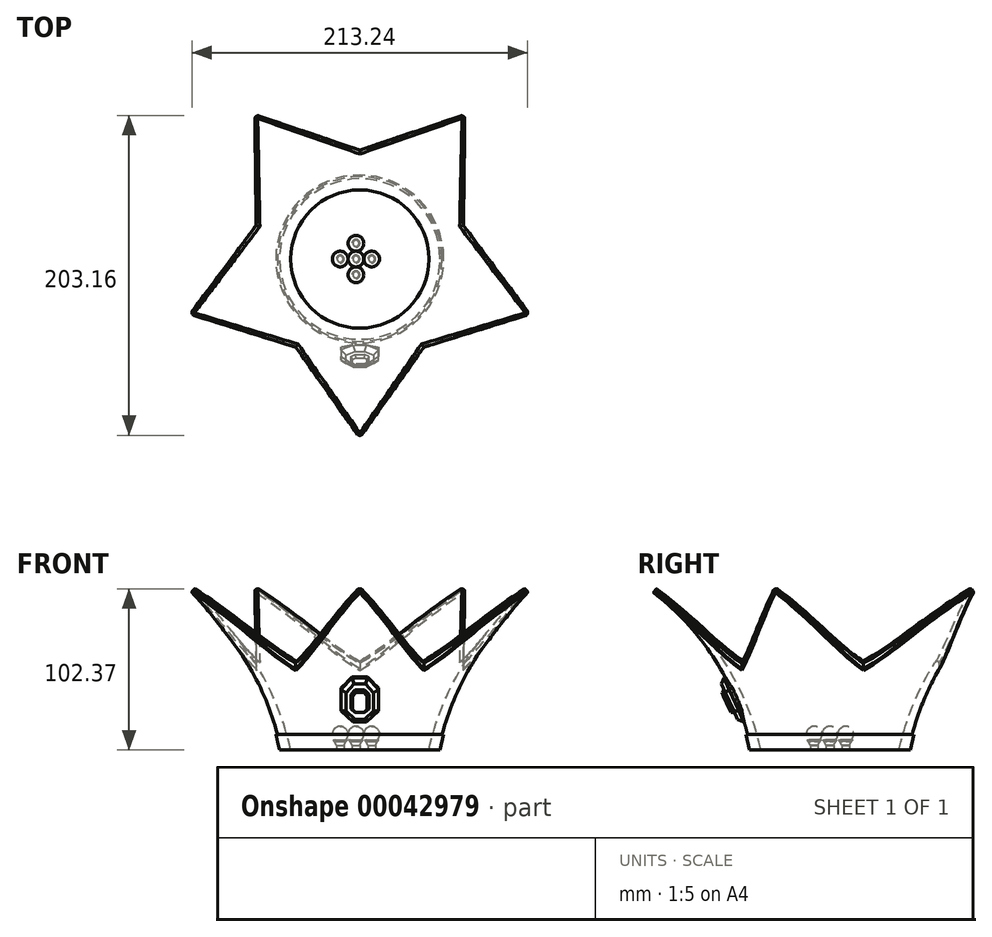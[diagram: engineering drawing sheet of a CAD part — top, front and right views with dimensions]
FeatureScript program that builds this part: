
annotation { "Feature Type Name" : "Feature", "Feature Type Description" : "" }
export const myFeature = defineFeature(function(context is Context, id is Id, definition is map)
    precondition{}
    {
        {
            var Q0;
            Q0=qCreatedBy(makeId("Front.planeOp"),FACE);
            var sketch = newSketch(context, id + "F0", { "sketchPlane" : qUnion([Q0])});
            skLineSegment(sketch, "E0", {"start": v(0, 0) * mm, "end": v(0, 100) * mm, "construction": true});
            skLineSegment(sketch, "E1", {"start": v(0, 0) * mm, "end": v(-50, 0) * mm, "construction": true});
            skArc(sketch, "E2", {"start": v(-50, 0) * mm, "mid": v(-71.94, 55.6) * mm, "end": v(-111.98, 100) * mm});
            skLineSegment(sketch, "E3", {"start": v(-111.98, 100) * mm, "end": v(-214.57, -32.8) * mm, "construction": true});
            skLineSegment(sketch, "E4", {"start": v(-111.98, 100) * mm, "end": v(-110.15, 102.37) * mm});
            skArc(sketch, "E5", {"start": v(-43.88, 0) * mm, "mid": v(-67.74, 57.2) * mm, "end": v(-110.15, 102.37) * mm});
            skLineSegment(sketch, "E6", {"start": v(-50, 0) * mm, "end": v(-43.88, 0) * mm});
            skLineSegment(sketch, "E7", {"start": v(-50, 0) * mm, "end": v(-51, 0) * mm});
            skLineSegment(sketch, "E8", {"start": v(-52.31, 10) * mm, "end": v(-53.31, 10) * mm});
            skLineSegment(sketch, "E9", {"start": v(-53.31, 10) * mm, "end": v(-51, 0) * mm});
            skLineSegment(sketch, "E10", {"start": v(-53.31, 10) * mm, "end": v(-53.31, 0) * mm, "construction": true});
            skSolve(sketch);
        }
        {
            var Q0;
            Q0=qSketchRegion(id+"F0",true);
            var Q1;
            Q1=sQuery(id+"F0.wireOp",EDGE,"E0");
            revolve(context, id + "F1", {"entities" : qUnion([Q0]), "axis" : qUnion([Q1]), "revolveType" : RevolveType.FULL});
        }
        {
            var Q0;
            Q0=qCreatedBy(makeId("Top.planeOp"),FACE);
            var sketch = newSketch(context, id + "F2", { "sketchPlane" : qUnion([Q0])});
            skLineSegment(sketch, "E11", {"start": v(0, 0) * mm, "end": v(0, -111.98) * mm, "construction": true});
            skCircle(sketch, "E12.0", {"center": v(0, 0) * mm, "radius": 111.98 * mm, "construction": true});
            skLineSegment(sketch, "E13", {"start": v(-1, -111.98) * mm, "end": v(1, -111.98) * mm});
            skLineSegment(sketch, "E14", {"start": v(-1, -111.98) * mm, "end": v(-40.68, -56) * mm});
            skPoint(sketch, "E15", {"position": v(0, -56) * mm});
            skLineSegment(sketch, "E16.MirrorCS", {"start": v(1, -111.98) * mm, "end": v(40.68, -56) * mm});
            skLineSegment(sketch, "E17.1.0", {"start": v(106.2, -35.56) * mm, "end": v(106.8, -33.65) * mm});
            skLineSegment(sketch, "E17.1.1", {"start": v(106.2, -35.56) * mm, "end": v(40.68, -56) * mm});
            skLineSegment(sketch, "E17.1.2", {"start": v(106.8, -33.65) * mm, "end": v(65.82, 21.39) * mm});
            skLineSegment(sketch, "E17.2.0", {"start": v(66.63, 90) * mm, "end": v(65.01, 91.18) * mm});
            skLineSegment(sketch, "E17.2.1", {"start": v(66.63, 90) * mm, "end": v(65.82, 21.39) * mm});
            skLineSegment(sketch, "E17.2.2", {"start": v(65.01, 91.18) * mm, "end": v(0, 69.2) * mm});
            skLineSegment(sketch, "E17.3.0", {"start": v(-65.01, 91.18) * mm, "end": v(-66.63, 90) * mm});
            skLineSegment(sketch, "E17.3.1", {"start": v(-65.01, 91.18) * mm, "end": v(0, 69.2) * mm});
            skLineSegment(sketch, "E17.3.2", {"start": v(-66.63, 90) * mm, "end": v(-65.82, 21.39) * mm});
            skLineSegment(sketch, "E17.4.0", {"start": v(-106.8, -33.65) * mm, "end": v(-106.2, -35.56) * mm});
            skLineSegment(sketch, "E17.4.1", {"start": v(-106.8, -33.65) * mm, "end": v(-65.82, 21.39) * mm});
            skLineSegment(sketch, "E17.4.2", {"start": v(-106.2, -35.56) * mm, "end": v(-40.68, -56) * mm});
            skCircle(sketch, "E18", {"center": v(0, 0) * mm, "radius": 111.99 * mm});
            skCircle(sketch, "E19.0", {"center": v(0, 0) * mm, "radius": 51 * mm, "construction": true});
            skPoint(sketch, "E20", {"position": v(0, -51) * mm});
            skLineSegment(sketch, "E21", {"start": v(0, -56) * mm, "end": v(0, -67) * mm, "construction": true});
            skSolve(sketch);
        }
        {
            var Q0;
            {var subQ2=sQuery(id+"F2.wireOp",EDGE,"E14");Q0=makeQuery(id+"F2.imprint","IMPRINT",FACE,{"disambiguationData":[TD([[makeQuery(id+"F2.imprint","IMPRINT",EDGE,{"derivedFrom":subQ2}),1.0]])]});}
            var Q1;
            {var subQ2=sQuery(id+"F2.wireOp",EDGE,"E16.MirrorCS");Q1=makeQuery(id+"F2.imprint","IMPRINT",FACE,{"disambiguationData":[TD([[makeQuery(id+"F2.imprint","IMPRINT",EDGE,{"derivedFrom":subQ2}),-1.0]])]});}
            var Q2;
            {var subQ2=sQuery(id+"F2.wireOp",EDGE,"E17.1.2");Q2=makeQuery(id+"F2.imprint","IMPRINT",FACE,{"disambiguationData":[TD([[makeQuery(id+"F2.imprint","IMPRINT",EDGE,{"derivedFrom":subQ2}),-1.0]])]});}
            var Q3;
            {var subQ2=sQuery(id+"F2.wireOp",EDGE,"E17.3.2");Q3=makeQuery(id+"F2.imprint","IMPRINT",FACE,{"disambiguationData":[TD([[makeQuery(id+"F2.imprint","IMPRINT",EDGE,{"derivedFrom":subQ2}),-1.0]])]});}
            var Q4;
            {var subQ2=sQuery(id+"F2.wireOp",EDGE,"E17.2.2");Q4=makeQuery(id+"F2.imprint","IMPRINT",FACE,{"disambiguationData":[TD([[makeQuery(id+"F2.imprint","IMPRINT",EDGE,{"derivedFrom":subQ2}),-1.0]])]});}
            extrude(context, id + "F3", {"entities" : qUnion([Q0, Q1, Q2, Q3, Q4]), "operationType" : NewBodyOperationType.REMOVE, "endBound" : BoundingType.THROUGH_ALL, "depth" : 25 * mm});
        }
        {
            var Q0;
            Q0=makeQuery(id+"F3.boolean.opBoolean","INTERSECT",VERTEX,{"derivedFrom":[makeQuery(id+"F1.opRevolve","SWEPT_FACE",FACE,{"disambiguationData":[OSD([sQuery(id+"F0.wireOp",EDGE,"E2")])]}),makeQuery(id+"F1.opRevolve","SWEPT_FACE",FACE,{"disambiguationData":[OSD([sQuery(id+"F0.wireOp",EDGE,"E4")])]}),makeQuery(id+"F3.opExtrude","SWEPT_FACE",FACE,{"disambiguationData":[OSD([sQuery(id+"F2.wireOp",EDGE,"E14")])]})]});
            var Q1;
            Q1=makeQuery(id+"F3.boolean.opBoolean","INTERSECT",VERTEX,{"derivedFrom":[makeQuery(id+"F1.opRevolve","SWEPT_FACE",FACE,{"disambiguationData":[OSD([sQuery(id+"F0.wireOp",EDGE,"E2")])]}),makeQuery(id+"F1.opRevolve","SWEPT_FACE",FACE,{"disambiguationData":[OSD([sQuery(id+"F0.wireOp",EDGE,"E4")])]}),makeQuery(id+"F3.opExtrude","SWEPT_FACE",FACE,{"disambiguationData":[OSD([sQuery(id+"F2.wireOp",EDGE,"E16.MirrorCS")])]})]});
            var Q2;
            Q2=sQuery(id+"F2.wireOp",VERTEX,"E21.end");
            cPlane(context, id + "F4", {"entities" : qUnion([Q0, Q1, Q2]), "cplaneType" : CPlaneType.THREE_POINT, "offset" : 150 * mm, "width" : 150 * mm, "height" : 150 * mm});
        }
        {
            var Q0;
            Q0=qCreatedBy(id+"F4.planeOp",FACE);
            cPlane(context, id + "F5", {"entities" : qUnion([Q0]), "cplaneType" : CPlaneType.OFFSET, "offset" : 20 * mm, "oppositeDirection" : true, "width" : 150 * mm, "height" : 150 * mm});
        }
        {
            var Q0;
            Q0=qCreatedBy(id+"F5.planeOp",FACE);
            var sketch = newSketch(context, id + "F6", { "sketchPlane" : qUnion([Q0])});
            skLineSegment(sketch, "E22.0", {"start": v(0, 0) * mm, "end": v(0, 91.2) * mm, "construction": true});
            skLineSegment(sketch, "E23.0", {"start": v(-1, 45.94) * mm, "end": v(1, 45.94) * mm, "construction": true});
            skPoint(sketch, "E24.0", {"position": v(-40.68, 69.52) * mm});
            skPoint(sketch, "E25.0", {"position": v(40.68, 69.52) * mm});
            skLineSegment(sketch, "E26", {"start": v(-40.68, 69.52) * mm, "end": v(40.68, 69.52) * mm, "construction": true});
            skLineSegment(sketch, "E27", {"start": v(-5, 69.52) * mm, "end": v(5, 69.52) * mm});
            skPoint(sketch, "E28", {"position": v(0, 69.52) * mm});
            skLineSegment(sketch, "E29", {"start": v(-5, 69.52) * mm, "end": v(-11.83, 61.33) * mm});
            skLineSegment(sketch, "E30", {"start": v(-11.83, 61.33) * mm, "end": v(-11.83, 46.33) * mm});
            skLineSegment(sketch, "E31", {"start": v(-11.83, 46.33) * mm, "end": v(-4.17, 38.9) * mm});
            skLineSegment(sketch, "E32", {"start": v(-4.17, 38.9) * mm, "end": v(0, 38.9) * mm});
            skLineSegment(sketch, "E33.MirrorCS", {"start": v(5, 69.52) * mm, "end": v(11.83, 61.33) * mm});
            skLineSegment(sketch, "E34.MirrorCS", {"start": v(11.83, 61.33) * mm, "end": v(11.83, 46.33) * mm});
            skLineSegment(sketch, "E35.MirrorCS", {"start": v(11.83, 46.33) * mm, "end": v(4.17, 38.9) * mm});
            skLineSegment(sketch, "E36.MirrorCS", {"start": v(4.17, 38.9) * mm, "end": v(0, 38.9) * mm});
            skSolve(sketch);
        }
        {
            var Q0;
            Q0=qSketchRegion(id+"F6",true);
            extrude(context, id + "F7", {"entities" : qUnion([Q0]), "operationType" : NewBodyOperationType.ADD, "depth" : 4.5 * mm, "hasSecondDirection" : true, "secondDirectionOppositeDirection" : true, "secondDirectionDepth" : 1 * mm});
        }
        {
            var Q0;
            Q0=makeQuery(id+"F7.opExtrude","CAP_EDGE",EDGE,{"disambiguationData":[OSD([sQuery(id+"F6.wireOp",EDGE,"E27")])],"isStart":false});
            var Q1;
            Q1=makeQuery(id+"F7.opExtrude","CAP_EDGE",EDGE,{"disambiguationData":[OSD([sQuery(id+"F6.wireOp",EDGE,"E29")])],"isStart":false});
            var Q2;
            Q2=makeQuery(id+"F7.opExtrude","CAP_EDGE",EDGE,{"disambiguationData":[OSD([sQuery(id+"F6.wireOp",EDGE,"E33.MirrorCS")])],"isStart":false});
            var Q3;
            Q3=makeQuery(id+"F7.opExtrude","CAP_EDGE",EDGE,{"disambiguationData":[OSD([sQuery(id+"F6.wireOp",EDGE,"E34.MirrorCS")])],"isStart":false});
            var Q4;
            Q4=makeQuery(id+"F7.opExtrude","CAP_EDGE",EDGE,{"disambiguationData":[OSD([sQuery(id+"F6.wireOp",EDGE,"E35.MirrorCS")])],"isStart":false});
            var Q5;
            Q5=makeQuery(id+"F7.opExtrude","CAP_EDGE",EDGE,{"disambiguationData":[OSD([sQuery(id+"F6.wireOp",EDGE,"E31")])],"isStart":false});
            var Q6;
            Q6=makeQuery(id+"F7.opExtrude","CAP_EDGE",EDGE,{"disambiguationData":[OSD([sQuery(id+"F6.wireOp",EDGE,"E32"),sQuery(id+"F6.wireOp",EDGE,"E36.MirrorCS")])],"isStart":false});
            var Q7;
            Q7=makeQuery(id+"F7.opExtrude","CAP_EDGE",EDGE,{"disambiguationData":[OSD([sQuery(id+"F6.wireOp",EDGE,"E30")])],"isStart":false});
            chamfer(context, id + "F8", {"entities" : qUnion([Q0, Q1, Q2, Q3, Q4, Q5, Q6, Q7]), "width" : 3 * mm, "tangentPropagation" : true});
        }
        {
            var Q0;
            Q0=makeQuery(id+"F7.opExtrude","CAP_FACE",FACE,{"disambiguationData":[OSD([sQuery(id+"F6.wireOp",EDGE,"E27"),sQuery(id+"F6.wireOp",EDGE,"E29"),sQuery(id+"F6.wireOp",EDGE,"E30"),sQuery(id+"F6.wireOp",EDGE,"E31"),sQuery(id+"F6.wireOp",EDGE,"E32"),sQuery(id+"F6.wireOp",EDGE,"E33.MirrorCS"),sQuery(id+"F6.wireOp",EDGE,"E34.MirrorCS"),sQuery(id+"F6.wireOp",EDGE,"E35.MirrorCS"),sQuery(id+"F6.wireOp",EDGE,"E36.MirrorCS")])],"isStart":false});
            var sketch = newSketch(context, id + "F9", { "sketchPlane" : qUnion([Q0])});
            skLineSegment(sketch, "E37", {"start": v(-3, 62.47) * mm, "end": v(0, 62.47) * mm});
            skLineSegment(sketch, "E38", {"start": v(-3, 62.47) * mm, "end": v(-5.72, 59.21) * mm});
            skLineSegment(sketch, "E39", {"start": v(-5.72, 49.21) * mm, "end": v(-3, 46.58) * mm});
            skLineSegment(sketch, "E40", {"start": v(-3, 46.58) * mm, "end": v(0, 46.58) * mm});
            skLineSegment(sketch, "E41", {"start": v(0, 66.52) * mm, "end": v(0, 41.9) * mm, "construction": true});
            skLineSegment(sketch, "E42", {"start": v(-5.72, 54.21) * mm, "end": v(0, 54.21) * mm, "construction": true});
            skLineSegment(sketch, "E43", {"start": v(-5.72, 59.21) * mm, "end": v(-5.72, 49.21) * mm});
            skLineSegment(sketch, "E44.MirrorCS", {"start": v(3, 62.47) * mm, "end": v(0, 62.47) * mm});
            skLineSegment(sketch, "E45.MirrorCS", {"start": v(3, 62.47) * mm, "end": v(5.72, 59.21) * mm});
            skLineSegment(sketch, "E46.MirrorCS", {"start": v(5.72, 59.21) * mm, "end": v(5.72, 49.21) * mm});
            skLineSegment(sketch, "E47.MirrorCS", {"start": v(5.72, 49.21) * mm, "end": v(3, 46.58) * mm});
            skLineSegment(sketch, "E48.MirrorCS", {"start": v(3, 46.58) * mm, "end": v(0, 46.58) * mm});
            skSolve(sketch);
        }
        {
            var Q0;
            Q0=makeQuery(id+"F9.imprint","IMPRINT",FACE,{"disambiguationData":[TD([[makeQuery(id+"F9.imprint","IMPRINT",EDGE,{"derivedFrom":sQuery(id+"F9.wireOp",EDGE,"E37")}),1.0]])]});
            cPlane(context, id + "F10", {"entities" : qUnion([Q0]), "cplaneType" : CPlaneType.OFFSET, "offset" : 2 * mm, "width" : 150 * mm, "height" : 150 * mm});
        }
        {
            var Q0;
            Q0=qCreatedBy(id+"F10.planeOp",FACE);
            var sketch = newSketch(context, id + "F11", { "sketchPlane" : qUnion([Q0])});
            skLineSegment(sketch, "E49.0", {"start": v(-3, 62.47) * mm, "end": v(-5.72, 59.21) * mm, "construction": true});
            skLineSegment(sketch, "E50.0", {"start": v(-3, 62.47) * mm, "end": v(0, 62.47) * mm, "construction": true});
            skLineSegment(sketch, "E51.0", {"start": v(3, 62.47) * mm, "end": v(0, 62.47) * mm, "construction": true});
            skLineSegment(sketch, "E52.0", {"start": v(3, 62.47) * mm, "end": v(5.72, 59.21) * mm, "construction": true});
            skLineSegment(sketch, "E53.0", {"start": v(5.72, 59.21) * mm, "end": v(5.72, 49.21) * mm, "construction": true});
            skLineSegment(sketch, "E54.0", {"start": v(5.72, 49.21) * mm, "end": v(3, 46.58) * mm, "construction": true});
            skLineSegment(sketch, "E55.0", {"start": v(3, 46.58) * mm, "end": v(0, 46.58) * mm, "construction": true});
            skLineSegment(sketch, "E56.0", {"start": v(-3, 46.58) * mm, "end": v(0, 46.58) * mm, "construction": true});
            skLineSegment(sketch, "E57.0", {"start": v(-5.72, 49.21) * mm, "end": v(-3, 46.58) * mm, "construction": true});
            skLineSegment(sketch, "E58.0", {"start": v(-5.72, 59.21) * mm, "end": v(-5.72, 49.21) * mm, "construction": true});
            skLineSegment(sketch, "E59.0", {"start": v(-2.53, 61.47) * mm, "end": v(0, 61.47) * mm});
            skLineSegment(sketch, "E59.1", {"start": v(2.53, 61.47) * mm, "end": v(0, 61.47) * mm});
            skLineSegment(sketch, "E59.2", {"start": v(-2.53, 61.47) * mm, "end": v(-4.72, 58.85) * mm});
            skLineSegment(sketch, "E59.3", {"start": v(2.53, 61.47) * mm, "end": v(4.72, 58.85) * mm});
            skLineSegment(sketch, "E59.4", {"start": v(4.72, 58.85) * mm, "end": v(4.72, 49.63) * mm});
            skLineSegment(sketch, "E59.5", {"start": v(4.72, 49.63) * mm, "end": v(2.6, 47.58) * mm});
            skLineSegment(sketch, "E59.6", {"start": v(-4.72, 58.85) * mm, "end": v(-4.72, 49.63) * mm});
            skLineSegment(sketch, "E59.7", {"start": v(-4.72, 49.63) * mm, "end": v(-2.6, 47.58) * mm});
            skLineSegment(sketch, "E59.8", {"start": v(-2.6, 47.58) * mm, "end": v(0, 47.58) * mm});
            skLineSegment(sketch, "E59.9", {"start": v(2.6, 47.58) * mm, "end": v(0, 47.58) * mm});
            skSolve(sketch);
        }
        {
            var Q1;
            Q1=makeQuery(id+"F9.imprint","IMPRINT",FACE,{"disambiguationData":[TD([[makeQuery(id+"F9.imprint","IMPRINT",EDGE,{"derivedFrom":sQuery(id+"F9.wireOp",EDGE,"E37")}),-1.0]])]});
            var Q2;
            Q2=makeQuery(id+"F11.imprint","IMPRINT",FACE,{"disambiguationData":[TD([[makeQuery(id+"F11.imprint","IMPRINT",EDGE,{"derivedFrom":sQuery(id+"F11.wireOp",EDGE,"E59.0")}),-1.0]])]});
            loft(context, id + "F12", {"operationType" : NewBodyOperationType.ADD, "sheetProfilesArray" : [{ "sheetProfileEntities" : qUnion([Q1]) }, { "sheetProfileEntities" : qUnion([Q2]) }]});
        }
        {
            var Q0;
            Q0=makeQuery(id+"F3.boolean.opBoolean","INTERSECT",EDGE,{"derivedFrom":[makeQuery(id+"F1.opRevolve","SWEPT_FACE",FACE,{"disambiguationData":[OSD([sQuery(id+"F0.wireOp",EDGE,"E2")])]}),makeQuery(id+"F3.opExtrude","SWEPT_FACE",FACE,{"disambiguationData":[OSD([sQuery(id+"F2.wireOp",EDGE,"E16.MirrorCS")])]})]});
            var Q1;
            Q1=makeQuery(id+"F3.boolean.opBoolean","INTERSECT",EDGE,{"derivedFrom":[makeQuery(id+"F1.opRevolve","SWEPT_FACE",FACE,{"disambiguationData":[OSD([sQuery(id+"F0.wireOp",EDGE,"E2")])]}),makeQuery(id+"F3.opExtrude","SWEPT_FACE",FACE,{"disambiguationData":[OSD([sQuery(id+"F2.wireOp",EDGE,"E14")])]})]});
            var Q2;
            Q2=makeQuery(id+"F3.boolean.opBoolean","INTERSECT",EDGE,{"derivedFrom":[makeQuery(id+"F1.opRevolve","SWEPT_FACE",FACE,{"disambiguationData":[OSD([sQuery(id+"F0.wireOp",EDGE,"E5")])]}),makeQuery(id+"F3.opExtrude","SWEPT_FACE",FACE,{"disambiguationData":[OSD([sQuery(id+"F2.wireOp",EDGE,"E14")])]})]});
            var Q3;
            Q3=makeQuery(id+"F3.boolean.opBoolean","INTERSECT",EDGE,{"derivedFrom":[makeQuery(id+"F1.opRevolve","SWEPT_FACE",FACE,{"disambiguationData":[OSD([sQuery(id+"F0.wireOp",EDGE,"E5")])]}),makeQuery(id+"F3.opExtrude","SWEPT_FACE",FACE,{"disambiguationData":[OSD([sQuery(id+"F2.wireOp",EDGE,"E16.MirrorCS")])]})]});
            var Q4;
            Q4=makeQuery(id+"F3.boolean.opBoolean","INTERSECT",EDGE,{"derivedFrom":[makeQuery(id+"F1.opRevolve","SWEPT_FACE",FACE,{"disambiguationData":[OSD([sQuery(id+"F0.wireOp",EDGE,"E2")])]}),makeQuery(id+"F3.opExtrude","SWEPT_FACE",FACE,{"disambiguationData":[OSD([sQuery(id+"F2.wireOp",EDGE,"E17.4.2")])]})]});
            var Q5;
            Q5=makeQuery(id+"F3.boolean.opBoolean","INTERSECT",EDGE,{"derivedFrom":[makeQuery(id+"F1.opRevolve","SWEPT_FACE",FACE,{"disambiguationData":[OSD([sQuery(id+"F0.wireOp",EDGE,"E5")])]}),makeQuery(id+"F3.opExtrude","SWEPT_FACE",FACE,{"disambiguationData":[OSD([sQuery(id+"F2.wireOp",EDGE,"E17.4.2")])]})]});
            var Q6;
            Q6=makeQuery(id+"F3.boolean.opBoolean","INTERSECT",EDGE,{"derivedFrom":[makeQuery(id+"F1.opRevolve","SWEPT_FACE",FACE,{"disambiguationData":[OSD([sQuery(id+"F0.wireOp",EDGE,"E2")])]}),makeQuery(id+"F3.opExtrude","SWEPT_FACE",FACE,{"disambiguationData":[OSD([sQuery(id+"F2.wireOp",EDGE,"E17.4.1")])]})]});
            var Q7;
            Q7=makeQuery(id+"F3.boolean.opBoolean","INTERSECT",EDGE,{"derivedFrom":[makeQuery(id+"F1.opRevolve","SWEPT_FACE",FACE,{"disambiguationData":[OSD([sQuery(id+"F0.wireOp",EDGE,"E5")])]}),makeQuery(id+"F3.opExtrude","SWEPT_FACE",FACE,{"disambiguationData":[OSD([sQuery(id+"F2.wireOp",EDGE,"E17.4.1")])]})]});
            var Q8;
            Q8=makeQuery(id+"F3.boolean.opBoolean","INTERSECT",EDGE,{"derivedFrom":[makeQuery(id+"F1.opRevolve","SWEPT_FACE",FACE,{"disambiguationData":[OSD([sQuery(id+"F0.wireOp",EDGE,"E2")])]}),makeQuery(id+"F3.opExtrude","SWEPT_FACE",FACE,{"disambiguationData":[OSD([sQuery(id+"F2.wireOp",EDGE,"E17.3.2")])]})]});
            var Q9;
            Q9=makeQuery(id+"F3.boolean.opBoolean","INTERSECT",EDGE,{"derivedFrom":[makeQuery(id+"F1.opRevolve","SWEPT_FACE",FACE,{"disambiguationData":[OSD([sQuery(id+"F0.wireOp",EDGE,"E5")])]}),makeQuery(id+"F3.opExtrude","SWEPT_FACE",FACE,{"disambiguationData":[OSD([sQuery(id+"F2.wireOp",EDGE,"E17.3.2")])]})]});
            var Q10;
            Q10=makeQuery(id+"F3.boolean.opBoolean","INTERSECT",EDGE,{"derivedFrom":[makeQuery(id+"F1.opRevolve","SWEPT_FACE",FACE,{"disambiguationData":[OSD([sQuery(id+"F0.wireOp",EDGE,"E5")])]}),makeQuery(id+"F3.opExtrude","SWEPT_FACE",FACE,{"disambiguationData":[OSD([sQuery(id+"F2.wireOp",EDGE,"E17.1.1")])]})]});
            var Q11;
            Q11=makeQuery(id+"F3.boolean.opBoolean","INTERSECT",EDGE,{"derivedFrom":[makeQuery(id+"F1.opRevolve","SWEPT_FACE",FACE,{"disambiguationData":[OSD([sQuery(id+"F0.wireOp",EDGE,"E2")])]}),makeQuery(id+"F3.opExtrude","SWEPT_FACE",FACE,{"disambiguationData":[OSD([sQuery(id+"F2.wireOp",EDGE,"E17.1.1")])]})]});
            var Q12;
            Q12=makeQuery(id+"F3.boolean.opBoolean","INTERSECT",EDGE,{"derivedFrom":[makeQuery(id+"F1.opRevolve","SWEPT_FACE",FACE,{"disambiguationData":[OSD([sQuery(id+"F0.wireOp",EDGE,"E5")])]}),makeQuery(id+"F3.opExtrude","SWEPT_FACE",FACE,{"disambiguationData":[OSD([sQuery(id+"F2.wireOp",EDGE,"E17.1.2")])]})]});
            var Q13;
            Q13=makeQuery(id+"F3.boolean.opBoolean","INTERSECT",EDGE,{"derivedFrom":[makeQuery(id+"F1.opRevolve","SWEPT_FACE",FACE,{"disambiguationData":[OSD([sQuery(id+"F0.wireOp",EDGE,"E2")])]}),makeQuery(id+"F3.opExtrude","SWEPT_FACE",FACE,{"disambiguationData":[OSD([sQuery(id+"F2.wireOp",EDGE,"E17.1.2")])]})]});
            var Q14;
            Q14=makeQuery(id+"F3.boolean.opBoolean","INTERSECT",EDGE,{"derivedFrom":[makeQuery(id+"F1.opRevolve","SWEPT_FACE",FACE,{"disambiguationData":[OSD([sQuery(id+"F0.wireOp",EDGE,"E2")])]}),makeQuery(id+"F3.opExtrude","SWEPT_FACE",FACE,{"disambiguationData":[OSD([sQuery(id+"F2.wireOp",EDGE,"E17.2.1")])]})]});
            var Q15;
            Q15=makeQuery(id+"F3.boolean.opBoolean","INTERSECT",EDGE,{"derivedFrom":[makeQuery(id+"F1.opRevolve","SWEPT_FACE",FACE,{"disambiguationData":[OSD([sQuery(id+"F0.wireOp",EDGE,"E5")])]}),makeQuery(id+"F3.opExtrude","SWEPT_FACE",FACE,{"disambiguationData":[OSD([sQuery(id+"F2.wireOp",EDGE,"E17.2.1")])]})]});
            var Q16;
            Q16=makeQuery(id+"F3.boolean.opBoolean","INTERSECT",EDGE,{"derivedFrom":[makeQuery(id+"F1.opRevolve","SWEPT_FACE",FACE,{"disambiguationData":[OSD([sQuery(id+"F0.wireOp",EDGE,"E2")])]}),makeQuery(id+"F3.opExtrude","SWEPT_FACE",FACE,{"disambiguationData":[OSD([sQuery(id+"F2.wireOp",EDGE,"E17.2.2")])]})]});
            var Q17;
            Q17=makeQuery(id+"F3.boolean.opBoolean","INTERSECT",EDGE,{"derivedFrom":[makeQuery(id+"F1.opRevolve","SWEPT_FACE",FACE,{"disambiguationData":[OSD([sQuery(id+"F0.wireOp",EDGE,"E5")])]}),makeQuery(id+"F3.opExtrude","SWEPT_FACE",FACE,{"disambiguationData":[OSD([sQuery(id+"F2.wireOp",EDGE,"E17.2.2")])]})]});
            var Q18;
            Q18=makeQuery(id+"F3.boolean.opBoolean","INTERSECT",EDGE,{"derivedFrom":[makeQuery(id+"F1.opRevolve","SWEPT_FACE",FACE,{"disambiguationData":[OSD([sQuery(id+"F0.wireOp",EDGE,"E2")])]}),makeQuery(id+"F3.opExtrude","SWEPT_FACE",FACE,{"disambiguationData":[OSD([sQuery(id+"F2.wireOp",EDGE,"E17.3.1")])]})]});
            var Q19;
            Q19=makeQuery(id+"F3.boolean.opBoolean","INTERSECT",EDGE,{"derivedFrom":[makeQuery(id+"F1.opRevolve","SWEPT_FACE",FACE,{"disambiguationData":[OSD([sQuery(id+"F0.wireOp",EDGE,"E5")])]}),makeQuery(id+"F3.opExtrude","SWEPT_FACE",FACE,{"disambiguationData":[OSD([sQuery(id+"F2.wireOp",EDGE,"E17.3.1")])]})]});
            fillet(context, id + "F13", {"entities" : qUnion([Q0, Q1, Q2, Q3, Q4, Q5, Q6, Q7, Q8, Q9, Q10, Q11, Q12, Q13, Q14, Q15, Q16, Q17, Q18, Q19]), "radius" : 1.3 * mm, "tangentPropagation" : true, "allowEdgeOverflow" : false});
        }
        {
            var Q0;
            Q0=qCreatedBy(makeId("Front.planeOp"),FACE);
            var sketch = newSketch(context, id + "F14", { "sketchPlane" : qUnion([Q0])});
            skPoint(sketch, "E60.0", {"position": v(0, 0) * mm});
            skPoint(sketch, "E61.0", {"position": v(-4.9, 0) * mm});
            skLineSegment(sketch, "E62", {"start": v(0, 0) * mm, "end": v(-4.9, 0) * mm, "construction": true});
            skLineSegment(sketch, "E63", {"start": v(-2.45, 0) * mm, "end": v(-2.45, 15) * mm});
            skLineSegment(sketch, "E64", {"start": v(-2.45, 0) * mm, "end": v(0, 0) * mm});
            skLineSegment(sketch, "E65", {"start": v(0, 0) * mm, "end": v(0, 3) * mm});
            skArc(sketch, "E66", {"start": v(2.13, 6.53) * mm, "mid": v(0.94, 4.84) * mm, "end": v(0, 3) * mm});
            skArc(sketch, "E67", {"start": v(-0.49, 5.4) * mm, "mid": v(0.88, 5.83) * mm, "end": v(2.13, 6.53) * mm});
            skArc(sketch, "E68", {"start": v(-0.49, 5.4) * mm, "mid": v(2.45, 11) * mm, "end": v(-2.45, 15) * mm});
            skLineSegment(sketch, "E69", {"start": v(-0.49, 5.4) * mm, "end": v(-2.45, 5) * mm, "construction": true});
            skLineSegment(sketch, "E70", {"start": v(0, 3) * mm, "end": v(-0.49, 5.4) * mm, "construction": true});
            skSolve(sketch);
        }
        {
            var Q0;
            Q0=makeQuery(id+"F14.imprint","IMPRINT",FACE,{"disambiguationData":[TD([[makeQuery(id+"F14.imprint","IMPRINT",EDGE,{"derivedFrom":sQuery(id+"F14.wireOp",EDGE,"E63")}),-1.0]])]});
            var Q1;
            Q1=sQuery(id+"F14.wireOp",EDGE,"E63");
            revolve(context, id + "F15", {"entities" : qUnion([Q0]), "axis" : qUnion([Q1]), "revolveType" : RevolveType.FULL});
        }
        {
            var Q0;
            Q0=makeQuery(id+"F15.opRevolve","SWEPT_BODY",BODY,{"disambiguationData":[OSD([sQuery(id+"F14.wireOp",EDGE,"E63"),sQuery(id+"F14.wireOp",EDGE,"E64"),sQuery(id+"F14.wireOp",EDGE,"E65"),sQuery(id+"F14.wireOp",EDGE,"E66"),sQuery(id+"F14.wireOp",EDGE,"E67"),sQuery(id+"F14.wireOp",EDGE,"E68")])]});
            transform(context, id + "F16", {"entities" : qUnion([Q0]), "transformType" : TransformType.TRANSLATION_3D, "dx" : 10 * mm, "dy" : 0 * mm, "dz" : 0 * mm, "makeCopy" : true});
        }
        {
            var Q0;
            Q0=makeQuery(id+"F15.opRevolve","SWEPT_BODY",BODY,{"disambiguationData":[OSD([sQuery(id+"F14.wireOp",EDGE,"E63"),sQuery(id+"F14.wireOp",EDGE,"E64"),sQuery(id+"F14.wireOp",EDGE,"E65"),sQuery(id+"F14.wireOp",EDGE,"E66"),sQuery(id+"F14.wireOp",EDGE,"E67"),sQuery(id+"F14.wireOp",EDGE,"E68")])]});
            transform(context, id + "F17", {"entities" : qUnion([Q0]), "transformType" : TransformType.TRANSLATION_3D, "dx" : -10 * mm, "dy" : 0 * mm, "dz" : 0 * mm, "makeCopy" : true});
        }
        {
            var Q0;
            Q0=makeQuery(id+"F15.opRevolve","SWEPT_BODY",BODY,{"disambiguationData":[OSD([sQuery(id+"F14.wireOp",EDGE,"E63"),sQuery(id+"F14.wireOp",EDGE,"E64"),sQuery(id+"F14.wireOp",EDGE,"E65"),sQuery(id+"F14.wireOp",EDGE,"E66"),sQuery(id+"F14.wireOp",EDGE,"E67"),sQuery(id+"F14.wireOp",EDGE,"E68")])]});
            transform(context, id + "F18", {"entities" : qUnion([Q0]), "transformType" : TransformType.TRANSLATION_3D, "dx" : 0 * mm, "dy" : 10 * mm, "dz" : 0 * mm, "makeCopy" : true});
        }
        {
            var Q0;
            Q0=makeQuery(id+"F15.opRevolve","SWEPT_BODY",BODY,{"disambiguationData":[OSD([sQuery(id+"F14.wireOp",EDGE,"E63"),sQuery(id+"F14.wireOp",EDGE,"E64"),sQuery(id+"F14.wireOp",EDGE,"E65"),sQuery(id+"F14.wireOp",EDGE,"E66"),sQuery(id+"F14.wireOp",EDGE,"E67"),sQuery(id+"F14.wireOp",EDGE,"E68")])]});
            transform(context, id + "F19", {"entities" : qUnion([Q0]), "transformType" : TransformType.TRANSLATION_3D, "dx" : 0 * mm, "dy" : -10 * mm, "dz" : 0 * mm, "makeCopy" : true});
        }
    });
